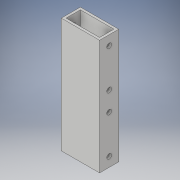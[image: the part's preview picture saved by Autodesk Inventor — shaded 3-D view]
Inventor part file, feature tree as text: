
AUTODESK INVENTOR PART (.ipt)
format: ipt  version: 2017 (Build 210142000, 142)  size: 121,856 bytes
history: native  units: in
note: dims shown in document units (in); Inventor stores cm internally (conversion verified against a paired STEP export)
features: sketch x2, extrude x1, hole x1
ambient origin geometry x8: Origin, YZ Plane, XZ Plane, XY Plane, X Axis, Y Axis, Z Axis, Center Point
bodies: Solid1 (feature_tree)
feature tree (4):
  extrude  "Extrusion1"  Depth=1.0in
  hole  "Hole2"  [1 undecoded]
  sketch  "Sketch1"  dims[d0=2.0in d1=1.0in]
  sketch  "Sketch2"  dims[d2=1.75in d3=0.75in d4=0.125in d5=0.125in d6=6.0in d7=0.0in d8=0.25in d9=0.5in d10=0.25in d11=0.5in d19=0.25in d20=0.75in d21=0.375in d22=0.25in d23=0.5635in d24=1.0in d25=0.8108in]
note: 1 required parameter value undecoded (feature->parameter linkage not recoverable at this tier; creation-order binding heuristic only, values carry confidence <= 0.55)
